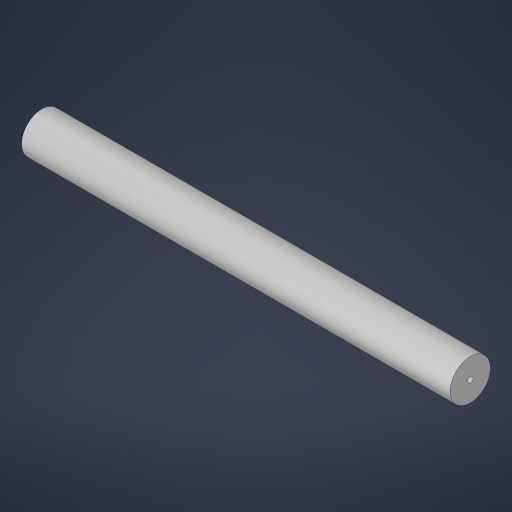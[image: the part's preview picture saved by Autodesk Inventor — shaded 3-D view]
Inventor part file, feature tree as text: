
AUTODESK INVENTOR PART (.ipt)
format: ipt  version: 2023.4 (Build 274418000, 418)  size: 183,296 bytes
history: native  units: in
note: dims shown in document units (in); Inventor stores cm internally (conversion verified against a paired STEP export)
features: sketch x4, hole x2, extrude x1
ambient origin geometry x8: Origin, YZ Plane, XZ Plane, XY Plane, X Axis, Y Axis, Z Axis, Center Point
bodies: Solid1 (feature_tree)
feature tree (7):
  sketch  "Sketch1"  dims[d0=1.125in d1=12.0in d2=0.0in]
  extrude  "Extrusion1"  Depth=12.0in TaperAngle=0.0deg
  sketch  "Sketch3"  dims[d10=0.156in d11=0.38in d12=0.375in d13=0.25in d14=0.5635in d15=0.536in d16=0.8108in]
  sketch  "Sketch4"
  hole  "Hole1"  [1 undecoded]
  hole  "Hole2"  [1 undecoded]
  sketch  "Sketch2"  dims[d3=0.156in d4=0.38in d5=0.385in d6=0.25in d7=0.5635in d8=0.536in d9=0.8108in]
note: 2 required parameter values undecoded (feature->parameter linkage not recoverable at this tier; creation-order binding heuristic only, values carry confidence <= 0.55)
